# Revit family: Sink-Undermount-Kitchen_Workstation-KOHLER-Riverby-K-24564_1
name_source: partatom
category: Plumbing Fixtures
units: mm (PartAtom-declared; Revit-internal decimal feet)

## family parameters
Cut with Voids When Loaded = No
Host = Face
OmniClass Number = 23.31.13.00
OmniClass Title = Sinks
Part Type = Normal
Room Calculation Point = No
Round Connector Dimension = Use Diameter
Shared = No

## types (8) — shared parameters
ADA Compliant = No
Assembly Code = D2010400
CW Connection = No
Cold Water Inlet = Cold Water Inlet
Date Modified = 06/15/2024
Default Elevation = 36"
Description = 35-3/4 Inch undermount Single-Bowl Farmhouse Workstation
Drain Included = No
HW Connection = No
Height = 9 13/16"
Hot Water Inlet = Hot Water Inlet
Length = 35 11/16"
Manufacturer = Kohler Co.
Master Format 2014 = 22 41 16
Master Format 2014 Name = Residential Lavatories and Sinks
Material = Enameled Cast Iron
Product Documentation Link = https://www.us.kohler.com
Product Name = Riverby
Product Page URL = http://www.us.kohler.com
URL = https://www.us.kohler.com
Vent Connection = No
Waste Connection = Yes
Waste Water Outlet = Waste Water Outlet
WaterSense Certified = No
Width = 20 7/8"

## per-type parameters (varying)
| type | Colander Finish | Drying Rack Finish | Finish | Model | Soaking Bin Finish | Type |
| 0-White | Kohler-Plastic-2LG-Light | Kohler-Plastic-3LG-Light | Kohler-Enameled_Cast_Iron-0-White | K-24564-PC-0 | Kohler-Plastic-1LG-Light | 1 |
| 58-Thunder Grey | Kohler-Plastic-2DK-Dark | Kohler-Plastic-3DK-Dark | KOHLER-Enameled_Cast_Iron-58-Thunder_Grey | K-24564-PC-58 | Kohler-Plastic-1DK-Dark | 2 |
| 7-Black Black | Kohler-Plastic-2DK-Dark | Kohler-Plastic-3DK-Dark | Kohler-Enameled_Cast_Iron-7-Black_Black | K-24564-PC-7 | Kohler-Plastic-1DK-Dark | 3 |
| 95-Ice Grey | Kohler-Plastic-2DK-Dark | Kohler-Plastic-3DK-Dark | KOHLER-Enameled_Cast_Iron-95-Ice_Grey | K-24564-PC-95 | Kohler-Plastic-1DK-Dark | 4 |
| 96-Biscuit | Kohler-Plastic-2LG-Light | Kohler-Plastic-3LG-Light | Kohler-Enameled_Cast_Iron-96-Biscuit | K-24564-PC-96 | Kohler-Plastic-1LG-Light | 5 |
| FF-Sea Salt | Kohler-Plastic-2LG-Light | Kohler-Plastic-3LG-Light | Kohler-Enameled_Cast_Iron-FF-Sea_Salt | K-24564-PC-FF | Kohler-Plastic-1LG-Light | 6 |
| NY-Dune | Kohler-Plastic-2LG-Light | Kohler-Plastic-3LG-Light | Kohler-Enameled_Cast_Iron-NY-Dune | K-24564-PC-NY | Kohler-Plastic-1LG-Light | 7 |
| TRF-Truffle | Kohler-Plastic-2LG-Light | Kohler-Plastic-3LG-Light | KOHLER-Enameled_Cast_Iron-TRF-Truffle | K-24564-PC-TRF | Kohler-Plastic-1LG-Light | 8 |

## geometry (parser evidence)
native form markers: Sweep x17
no freeform markers — native parametric forms only
